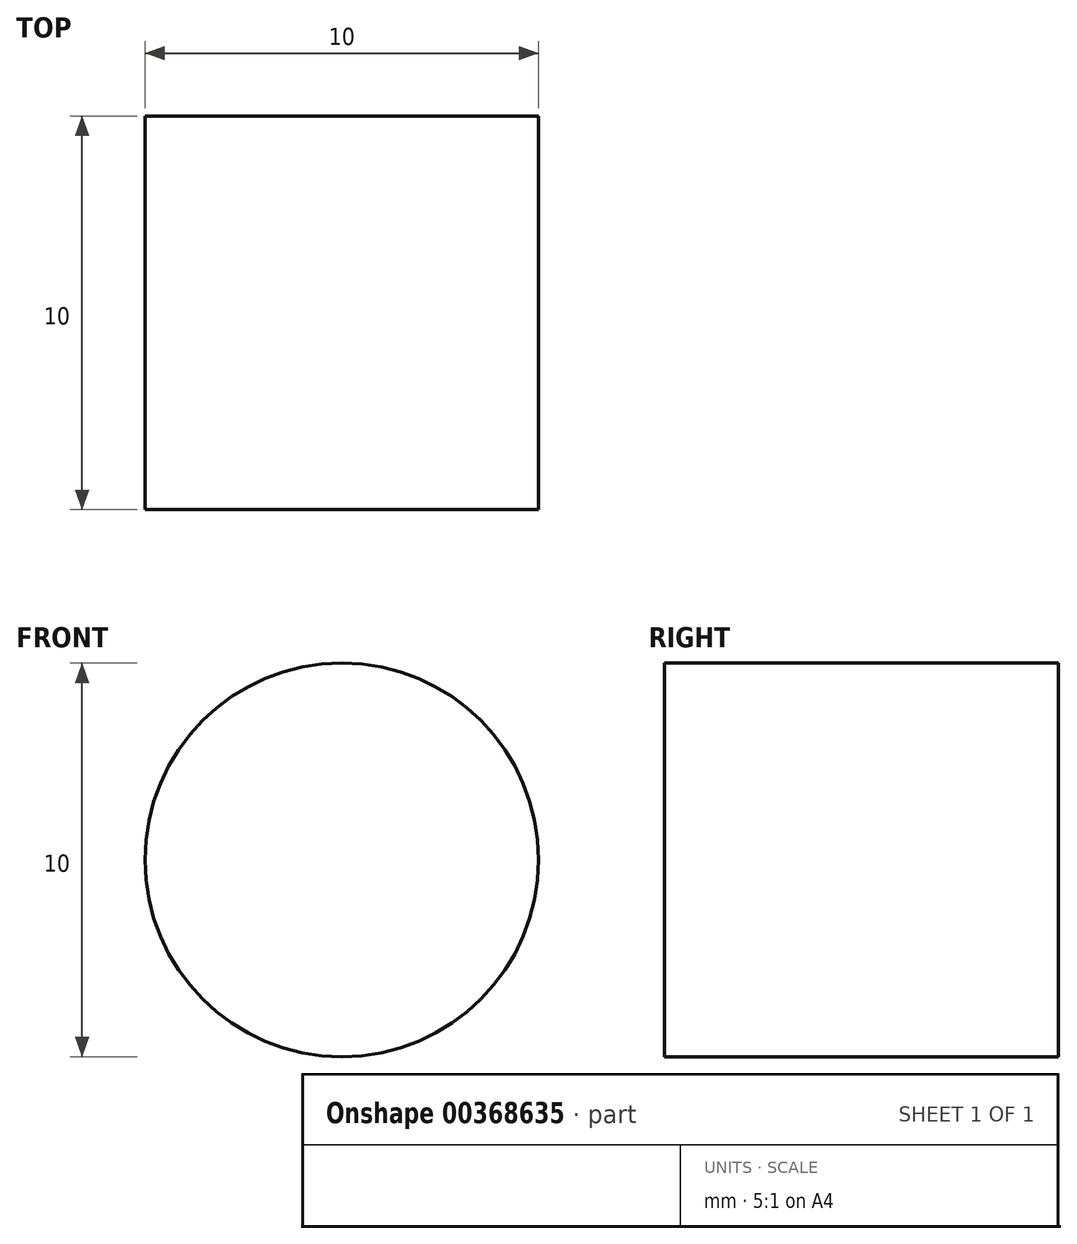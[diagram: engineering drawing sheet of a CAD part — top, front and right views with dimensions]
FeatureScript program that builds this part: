
annotation { "Feature Type Name" : "Feature", "Feature Type Description" : "" }
export const myFeature = defineFeature(function(context is Context, id is Id, definition is map)
    precondition{}
    {
        {
            var Q0;
            Q0=qCreatedBy(makeId("Front.planeOp"),FACE);
            var sketch = newSketch(context, id + "F0", { "sketchPlane" : qUnion([Q0])});
            skCircle(sketch, "E0", {"center": v(0, 0) * mm, "radius": 5 * mm});
            skSolve(sketch);
        }
        {
            var Q0;
            Q0 = qSketchRegion(id + "F0", true);
            extrude(context, id + "F1", {"entities" : qUnion([Q0]), "depth" : 10 * mm});
        }
    });
